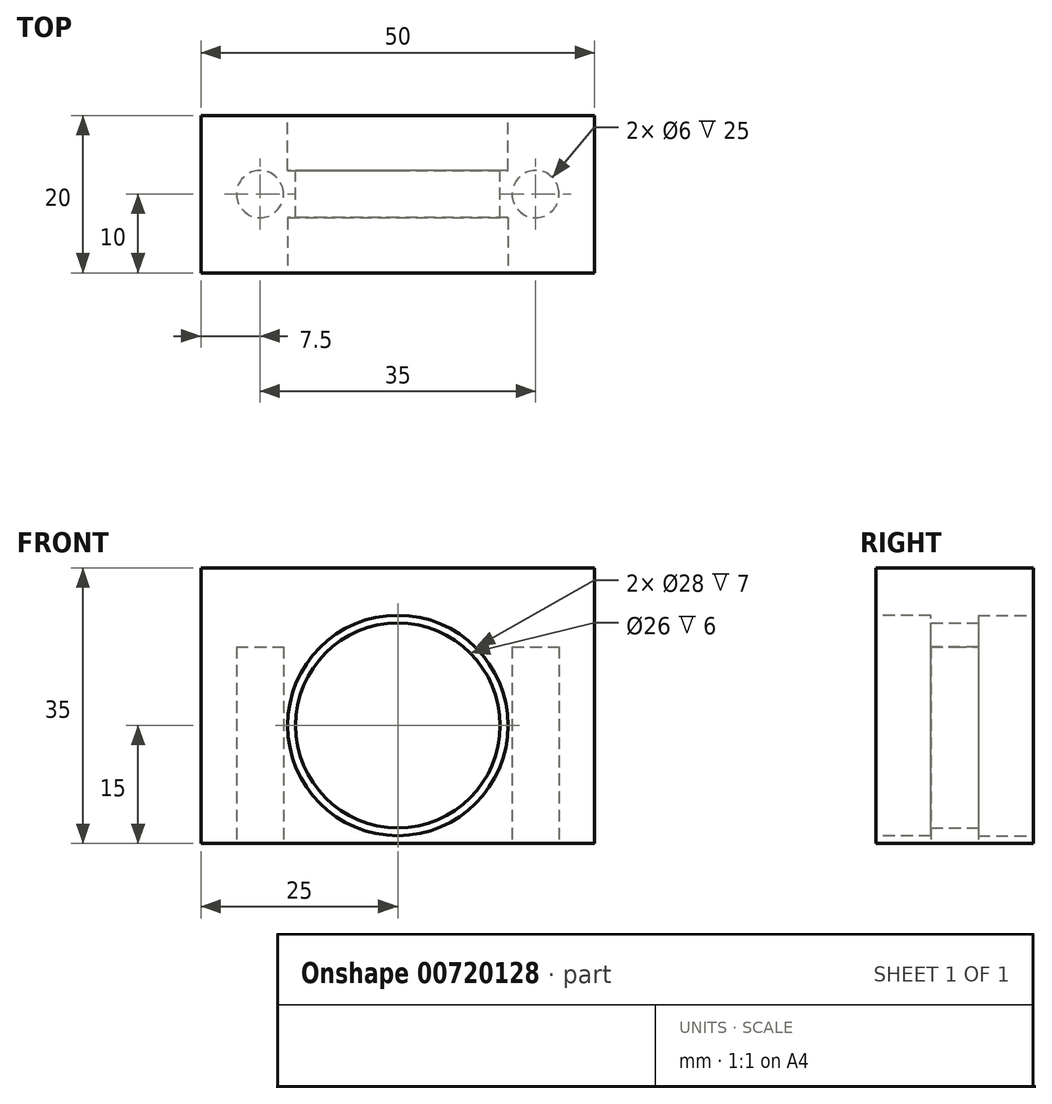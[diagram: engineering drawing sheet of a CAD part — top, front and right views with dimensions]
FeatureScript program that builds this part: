
annotation { "Feature Type Name" : "Feature", "Feature Type Description" : "" }
export const myFeature = defineFeature(function(context is Context, id is Id, definition is map)
    precondition{}
    {
        {
            var Q0;
            Q0=qCreatedBy(makeId("Front.planeOp"),FACE);
            var sketch = newSketch(context, id + "F0", { "sketchPlane" : qUnion([Q0])});
            skLineSegment(sketch, "E0.bottom", {"start": v(0, 0) * mm, "end": v(50, 0) * mm});
            skLineSegment(sketch, "E0.top", {"start": v(0, 35) * mm, "end": v(50, 35) * mm});
            skLineSegment(sketch, "E0.left", {"start": v(0, 0) * mm, "end": v(0, 35) * mm});
            skLineSegment(sketch, "E0.right", {"start": v(50, 0) * mm, "end": v(50, 35) * mm});
            skSolve(sketch);
        }
        {
            var Q0;
            Q0=makeQuery(id+"F0.imprint","IMPRINT",FACE,{"disambiguationData":[TD([[makeQuery(id+"F0.imprint","IMPRINT",EDGE,{"derivedFrom":sQuery(id+"F0.wireOp",EDGE,"E0.bottom")}),1.0]])]});
            extrude(context, id + "F1", {"entities" : qUnion([Q0]), "depth" : 20 * mm, "offsetDistance" : 25 * mm});
        }
        {
            var Q0;
            Q0=makeQuery(id+"F1.opExtrude","CAP_FACE",FACE,{"disambiguationData":[OSD([sQuery(id+"F0.wireOp",EDGE,"E0.bottom"),sQuery(id+"F0.wireOp",EDGE,"E0.top"),sQuery(id+"F0.wireOp",EDGE,"E0.left"),sQuery(id+"F0.wireOp",EDGE,"E0.right")])],"isStart":false});
            var sketch = newSketch(context, id + "F2", { "sketchPlane" : qUnion([Q0])});
            skCircle(sketch, "E1", {"center": v(25, 15) * mm, "radius": 14 * mm});
            skPoint(sketch, "E1.centerSnap0", {"position": v(25, 0) * mm});
            skSolve(sketch);
        }
        {
            var Q0;
            Q0=makeQuery(id+"F2.imprint","IMPRINT",FACE,{"disambiguationData":[TD([[makeQuery(id+"F2.imprint","IMPRINT",EDGE,{"derivedFrom":sQuery(id+"F2.wireOp",EDGE,"E1")}),1.0]])]});
            extrude(context, id + "F3", {"entities" : qUnion([Q0]), "operationType" : NewBodyOperationType.REMOVE, "oppositeDirection" : true, "depth" : 7 * mm, "offsetDistance" : 25 * mm});
        }
        {
            var Q0;
            Q0=makeQuery(id+"F1.opExtrude","CAP_FACE",FACE,{"disambiguationData":[OSD([sQuery(id+"F0.wireOp",EDGE,"E0.bottom"),sQuery(id+"F0.wireOp",EDGE,"E0.top"),sQuery(id+"F0.wireOp",EDGE,"E0.left"),sQuery(id+"F0.wireOp",EDGE,"E0.right")])],"isStart":true});
            var sketch = newSketch(context, id + "F4", { "sketchPlane" : qUnion([Q0])});
            skCircle(sketch, "E2", {"center": v(-25, 15) * mm, "radius": 14 * mm});
            skPoint(sketch, "E2.centerSnap0", {"position": v(-25, 0) * mm});
            skSolve(sketch);
        }
        {
            var Q0;
            Q0=makeQuery(id+"F4.imprint","IMPRINT",FACE,{"disambiguationData":[TD([[makeQuery(id+"F4.imprint","IMPRINT",EDGE,{"derivedFrom":sQuery(id+"F4.wireOp",EDGE,"E2")}),1.0]])]});
            extrude(context, id + "F5", {"entities" : qUnion([Q0]), "operationType" : NewBodyOperationType.REMOVE, "oppositeDirection" : true, "depth" : 7 * mm, "offsetDistance" : 25 * mm});
        }
        {
            var Q0;
            Q0=makeQuery(id+"F5.boolean.opBoolean","COPY",FACE,{"derivedFrom":makeQuery(id+"F5.opExtrude","CAP_FACE",FACE,{"disambiguationData":[OSD([sQuery(id+"F4.wireOp",EDGE,"E2")])],"isStart":false})});
            var sketch = newSketch(context, id + "F6", { "sketchPlane" : qUnion([Q0])});
            skCircle(sketch, "E3", {"center": v(-25, 15) * mm, "radius": 13 * mm});
            skSolve(sketch);
        }
        {
            var Q0;
            Q0=makeQuery(id+"F6.imprint","IMPRINT",FACE,{"disambiguationData":[TD([[makeQuery(id+"F6.imprint","IMPRINT",EDGE,{"derivedFrom":sQuery(id+"F6.wireOp",EDGE,"E3")}),1.0]])]});
            extrude(context, id + "F7", {"entities" : qUnion([Q0]), "operationType" : NewBodyOperationType.REMOVE, "endBound" : BoundingType.THROUGH_ALL, "oppositeDirection" : true, "depth" : 25 * mm, "offsetDistance" : 25 * mm});
        }
        {
            var Q0;
            Q0=makeQuery(id+"F1.opExtrude","SWEPT_FACE",FACE,{"disambiguationData":[OSD([sQuery(id+"F0.wireOp",EDGE,"E0.bottom")])]});
            var sketch = newSketch(context, id + "F8", { "sketchPlane" : qUnion([Q0])});
            skCircle(sketch, "E4", {"center": v(7.5, 10) * mm, "radius": 3 * mm});
            skPoint(sketch, "E4.centerSnap0", {"position": v(0, 10) * mm});
            skCircle(sketch, "E5", {"center": v(42.5, 10) * mm, "radius": 3 * mm});
            skSolve(sketch);
        }
        {
            var Q0;
            Q0=makeQuery(id+"F8.imprint","IMPRINT",FACE,{"disambiguationData":[TD([[makeQuery(id+"F8.imprint","IMPRINT",EDGE,{"derivedFrom":sQuery(id+"F8.wireOp",EDGE,"E4")}),1.0]])]});
            var Q1;
            Q1=makeQuery(id+"F8.imprint","IMPRINT",FACE,{"disambiguationData":[TD([[makeQuery(id+"F8.imprint","IMPRINT",EDGE,{"derivedFrom":sQuery(id+"F8.wireOp",EDGE,"E5")}),1.0]])]});
            extrude(context, id + "F9", {"entities" : qUnion([Q0, Q1]), "operationType" : NewBodyOperationType.REMOVE, "oppositeDirection" : true, "depth" : 25 * mm, "offsetDistance" : 25 * mm});
        }
    });
